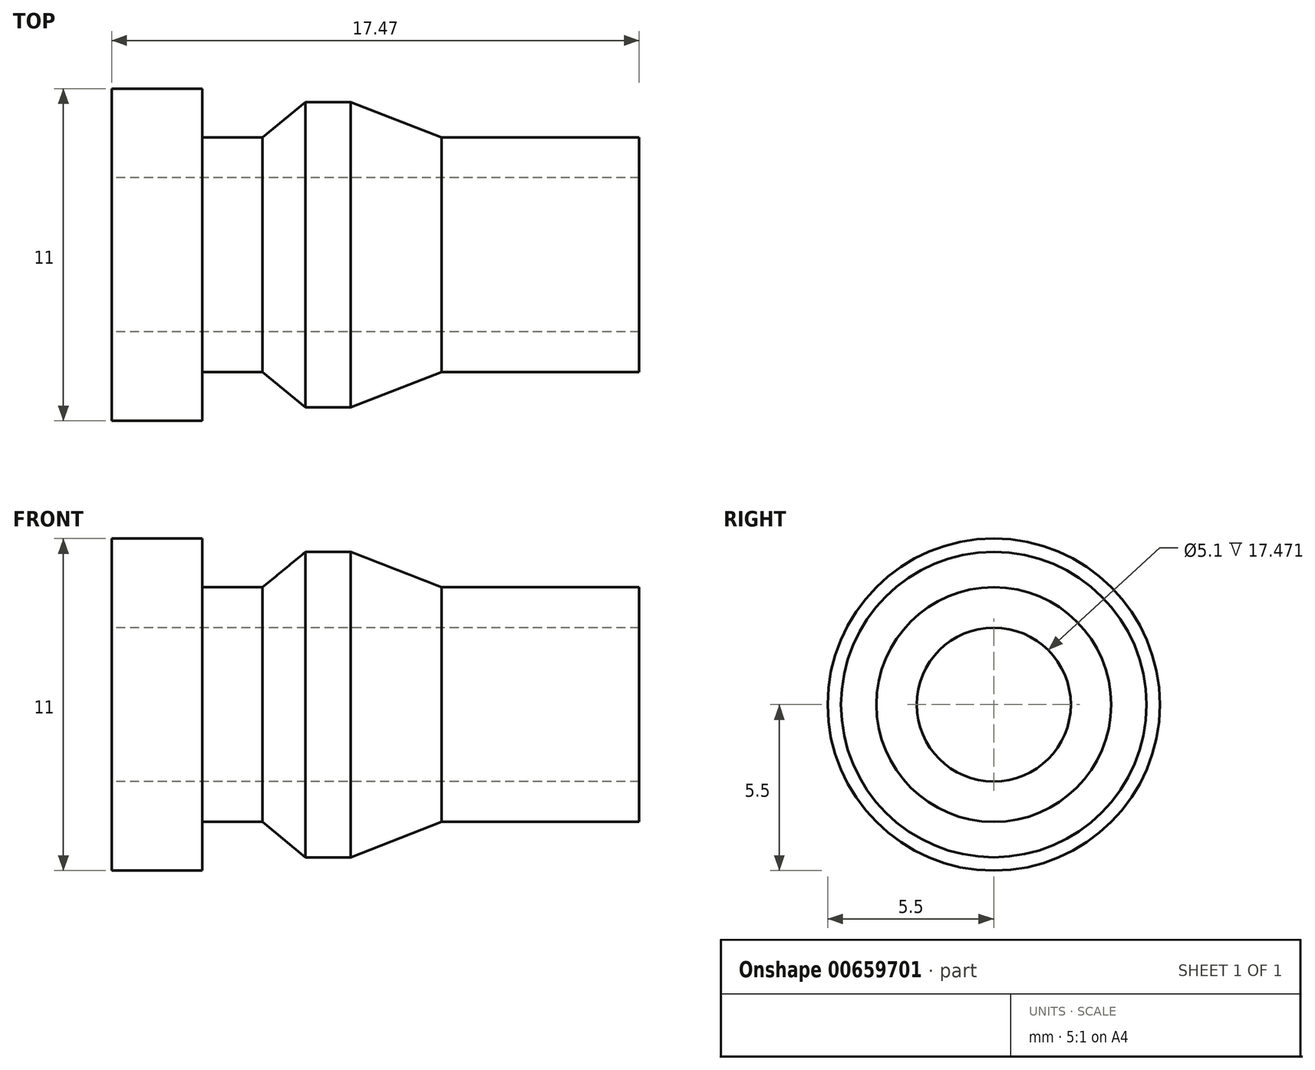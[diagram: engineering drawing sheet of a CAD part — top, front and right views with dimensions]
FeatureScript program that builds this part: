
annotation { "Feature Type Name" : "Feature", "Feature Type Description" : "" }
export const myFeature = defineFeature(function(context is Context, id is Id, definition is map)
    precondition{}
    {
        {
            var Q0;
            Q0=qCreatedBy(makeId("Front.planeOp"),FACE);
            var sketch = newSketch(context, id + "F0", { "sketchPlane" : qUnion([Q0])});
            skLineSegment(sketch, "E0", {"start": v(0, 2.55) * mm, "end": v(0, 5.5) * mm});
            skLineSegment(sketch, "E1", {"start": v(0, 5.5) * mm, "end": v(3, 5.5) * mm});
            skLineSegment(sketch, "E2", {"start": v(3, 5.5) * mm, "end": v(3, 3.89) * mm});
            skLineSegment(sketch, "E3", {"start": v(3, 3.89) * mm, "end": v(5, 3.89) * mm});
            skLineSegment(sketch, "E4", {"start": v(5, 3.89) * mm, "end": v(6.42, 5.06) * mm});
            skLineSegment(sketch, "E5", {"start": v(10.92, 3.89) * mm, "end": v(17.47, 3.89) * mm});
            skLineSegment(sketch, "E6", {"start": v(17.47, 3.89) * mm, "end": v(17.47, 2.55) * mm});
            skLineSegment(sketch, "E7", {"start": v(17.47, 2.55) * mm, "end": v(0, 2.55) * mm});
            skLineSegment(sketch, "E8", {"start": v(-4.3, 0) * mm, "end": v(17.1, 0) * mm});
            skLineSegment(sketch, "E9", {"start": v(6.42, 5.06) * mm, "end": v(7.92, 5.06) * mm});
            skLineSegment(sketch, "E10", {"start": v(7.92, 5.06) * mm, "end": v(10.92, 3.89) * mm});
            skSolve(sketch);
        }
        {
            var Q0;
            Q0=makeQuery(id+"F0.imprint","IMPRINT",FACE,{"disambiguationData":[TD([[makeQuery(id+"F0.imprint","IMPRINT",EDGE,{"derivedFrom":sQuery(id+"F0.wireOp",EDGE,"E0")}),-1.0]])]});
            var Q1;
            Q1=sQuery(id+"F0.wireOp",EDGE,"E8");
            revolve(context, id + "F1", {"entities" : qUnion([Q0]), "axis" : qUnion([Q1]), "revolveType" : RevolveType.FULL});
        }
    });
